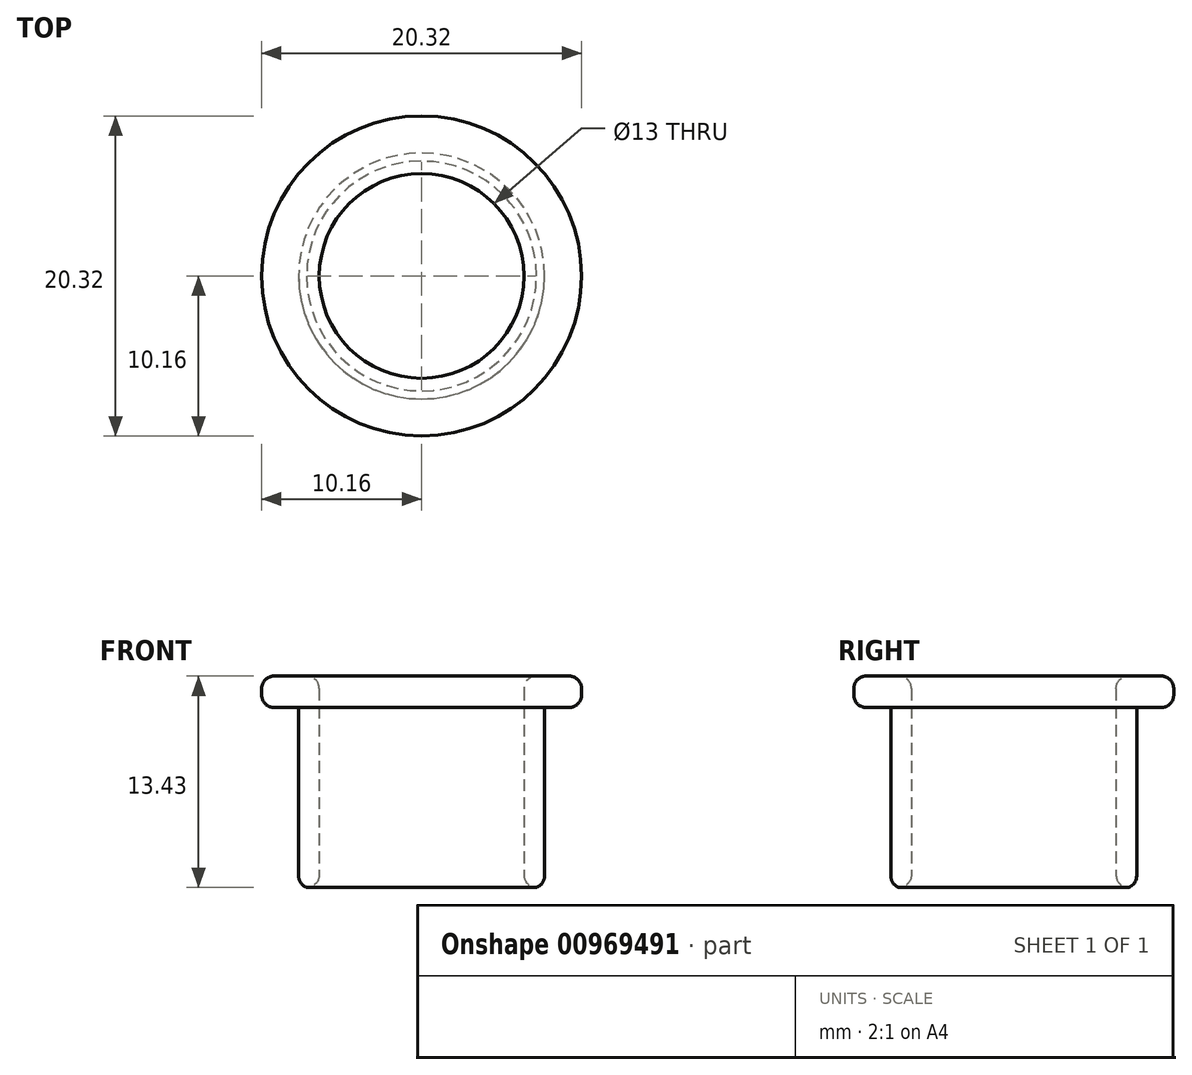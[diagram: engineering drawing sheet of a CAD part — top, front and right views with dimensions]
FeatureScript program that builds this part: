
annotation { "Feature Type Name" : "Feature", "Feature Type Description" : "" }
export const myFeature = defineFeature(function(context is Context, id is Id, definition is map)
    precondition{}
    {
        {
            var Q0;
            Q0=qCreatedBy(makeId("Top.planeOp"),FACE);
            var sketch = newSketch(context, id + "F0", { "sketchPlane" : qUnion([Q0])});
            skCircle(sketch, "E0", {"center": v(0, 0) * mm, "radius": 6.5 * mm});
            skCircle(sketch, "E1", {"center": v(0, 0) * mm, "radius": 7.81 * mm});
            skSolve(sketch);
        }
        {
            var Q0;
            Q0=qSketchRegion(id+"F0",true);
            extrude(context, id + "F1", {"entities" : qUnion([Q0]), "depth" : 11.43 * mm, "offsetDistance" : 25 * mm});
        }
        {
            var Q0;
            Q0=makeQuery(id+"F1.opExtrude","CAP_FACE",FACE,{"disambiguationData":[OSD([sQuery(id+"F0.wireOp",EDGE,"E0"),sQuery(id+"F0.wireOp",EDGE,"E1")])],"isStart":false});
            var sketch = newSketch(context, id + "F2", { "sketchPlane" : qUnion([Q0])});
            skCircle(sketch, "E2", {"center": v(0, 0) * mm, "radius": 10.16 * mm});
            skCircle(sketch, "E3", {"center": v(0, 0) * mm, "radius": 6.5 * mm});
            skSolve(sketch);
        }
        {
            var Q0;
            Q0=qSketchRegion(id+"F2",true);
            extrude(context, id + "F3", {"entities" : qUnion([Q0]), "operationType" : NewBodyOperationType.ADD, "depth" : 2 * mm, "offsetDistance" : 25 * mm});
        }
        {
            var Q0;
            Q0=makeQuery(id+"F3.opExtrude","CAP_EDGE",EDGE,{"disambiguationData":[OSD([sQuery(id+"F2.wireOp",EDGE,"E3")])],"isStart":false});
            var Q1;
            Q1=makeQuery(id+"F1.opExtrude","CAP_EDGE",EDGE,{"disambiguationData":[OSD([sQuery(id+"F0.wireOp",EDGE,"E0")])],"isStart":true});
            var Q2;
            Q2=makeQuery(id+"F1.opExtrude","CAP_EDGE",EDGE,{"disambiguationData":[OSD([sQuery(id+"F0.wireOp",EDGE,"E1")])],"isStart":false});
            var Q3;
            Q3=makeQuery(id+"F3.opExtrude","CAP_EDGE",EDGE,{"disambiguationData":[OSD([sQuery(id+"F2.wireOp",EDGE,"E2")])],"isStart":false});
            fillet(context, id + "F4", {"entities" : qUnion([Q0, Q1, Q2, Q3]), "radius" : .8 * mm, "tangentPropagation" : true, "allowEdgeOverflow" : false});
        }
        {
            var Q0;
            Q0=makeQuery(id+"F1.opExtrude","CAP_EDGE",EDGE,{"disambiguationData":[OSD([sQuery(id+"F0.wireOp",EDGE,"E1")])],"isStart":true});
            var Q1;
            Q1=makeQuery(id+"F3.opExtrude","CAP_EDGE",EDGE,{"disambiguationData":[OSD([sQuery(id+"F2.wireOp",EDGE,"E2")])],"isStart":true});
            fillet(context, id + "F5", {"entities" : qUnion([Q0, Q1]), "radius" : .8 * mm, "tangentPropagation" : true, "allowEdgeOverflow" : false});
        }
    });
